# Revit family: Maxlogic Sounder, Beacon, Sounder Beacon (Ceiling type)
name_source: partatom
category: Fire Alarm Devices
units: mm (PartAtom-declared; Revit-internal decimal feet)

## family parameters
Cut with Voids When Loaded = No
Host = Face
Maintain Annotation Orientation = Yes
OmniClass Number = 23.85.30.21
OmniClass Title = Environmental Detection/Registration
Part Type = Normal
Room Calculation Point = No
Round Connector Dimension = Use Diameter
Shared = No

## types (6) — shared parameters
Code Performance = EN 54-23
Color = Red
Fax Number = (+)90 216 466 45 10
Flaşör = Yes
Flaşör,flaşörlü siren Tavan = Yes
Installation Manual = https://mavilielektronik.com
Main Material = Red Plastic PC/ABS
Manufacturer = Mavili Elektronik Ticaret A.Ş.
Model = Maxlogic
Mounting surface = Ceiling Mount
Nominal Depth = 82 mm
Operating temperature = (-25°C) - (+70°C)
Secondary Material = Plastic
Siren Tavan = No
URL = https://www.mavili.com.tr
Warranty Duration Labor = 2
Warranty Duration Parts = 2
Warranty Duration Unit = Year
zero-valued in all types: Cost, Default Elevation

## per-type parameters (varying)
| type | Description | Device Adress Setup | IP 33 Taban | IP 65 Taban | Mounting height | Nominal Height | Nominal Width | Operating voltage range | Operatonal Voltage (default) | Product Code | Protection Sign | Weight |
| Maxlogic Conventional Ceiling Type (Class C, IP33C) Beacon | Conventional Ceiling Type (Class C, IP33C) Beacon |  | Yes | No | 3 Meters | 95 mm | 95 mm | 21-28V/DC | 24 V/DC | ML-2421 | IP 33C | 149 gr |
| Maxlogic Conventional Ceiling Type (Class C, IP65) Beacon | Conventional Ceiling Type (Class C, IP65) Beacon |  | No | Yes | 3 Meters | 99 mm | 99 mm | 21-28V/DC | 24 V/DC | ML-2422 | IP 65 | 153 gr |
| Maxlogic Addressable Ceiling Type (Class C, IP33C) Beacon | Addressable Ceiling Type (Class C, IP33C) Beacon | The address is given to devices by addressable programmer | Yes | No | 3 Meters | 95 mm | 95 mm | 18-33V/DC | 26 V/DC | ML-1421 | IP 33C | 153 gr |
| Maxlogic Addressable Ceiling Type (Class C, IP65) Beacon | Addressable Ceiling Type (Class C, IP65) Beacon | The address is given to devices by addressable programmer | No | Yes | 3 meters | 99 mm | 99 mm | 18-33V/DC | 24 V/DC | ML-1422 | IP 65 | 153 gr |
| Maxlogic Addressable Ceiling Type (Class C, IP33C) Beacon With Short Circuit Isolator | Addressable Ceiling Type (Class C, IP33C) Beacon With Short Circuit Isolator | The address is given to devices by addressable programmer | Yes | No | 3 Meters | 95 mm | 95 mm | 18-33V/DC | 26 V/DC | ML-1421.SCI | IP 33C | 153 gr |
| Maxlogic Addressable Ceiling Type (Class C, IP65) Beacon With Short Circuit Isolator | Addressable Ceiling Type (Class C, IP65) Beacon With Short Circuit Isolator | The address is given to devices by addressable programmer | No | Yes | 3 meters | 99 mm | 99 mm | 18-33V/DC | 24 V/DC | ML-1422.SCI | IP 65 | 153 gr |

## geometry (parser evidence)
native form markers: Sweep x2
no freeform markers — native parametric forms only
